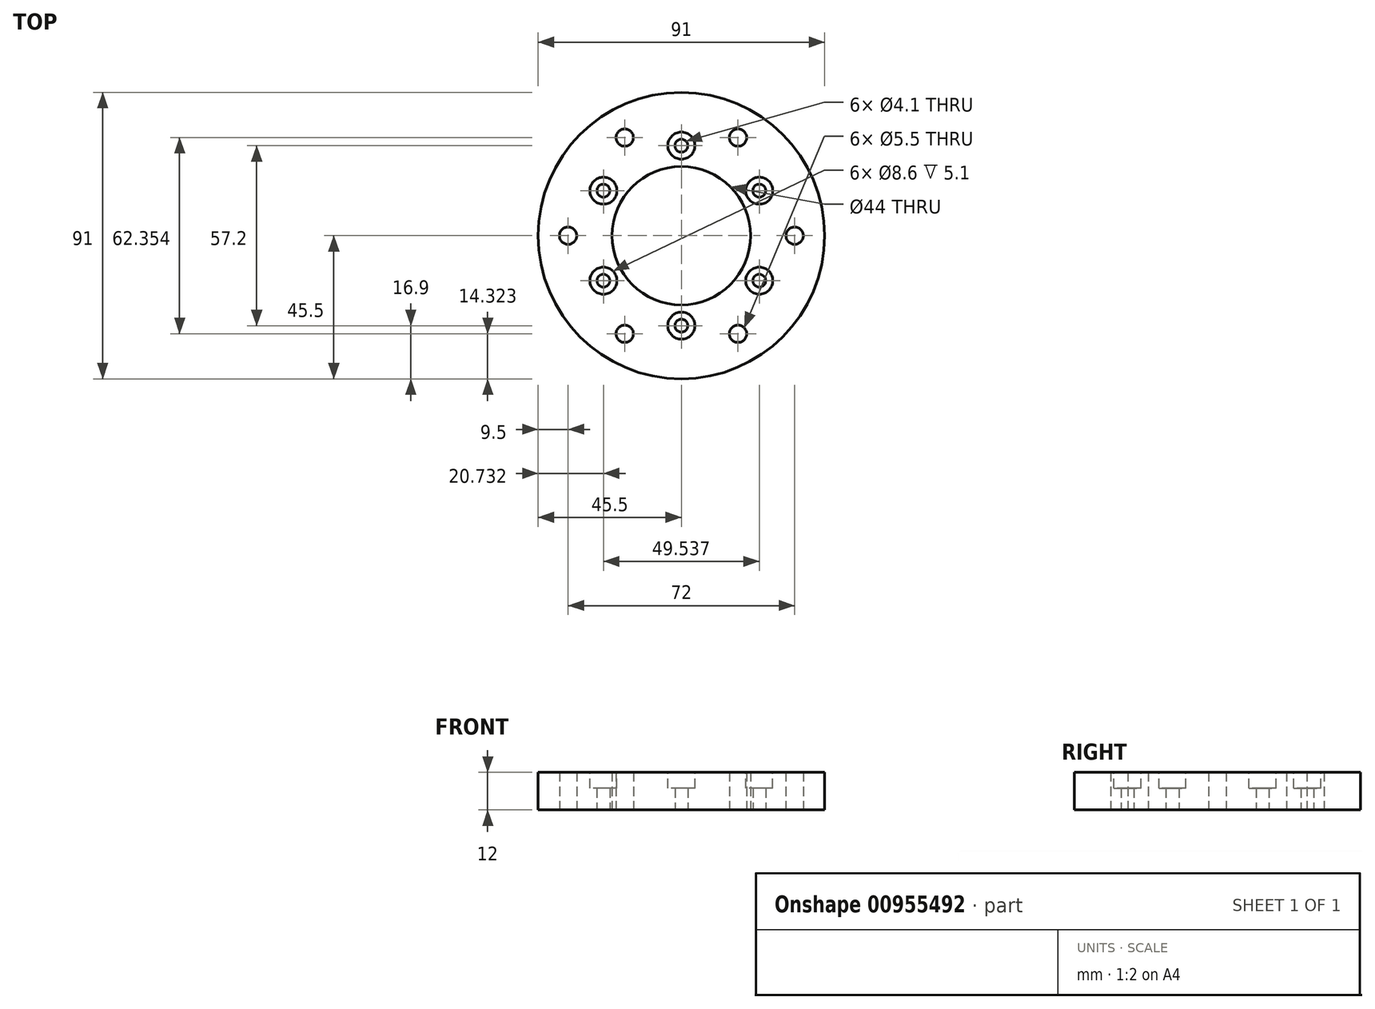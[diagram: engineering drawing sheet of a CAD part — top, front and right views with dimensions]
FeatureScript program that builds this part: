
annotation { "Feature Type Name" : "Feature", "Feature Type Description" : "" }
export const myFeature = defineFeature(function(context is Context, id is Id, definition is map)
    precondition{}
    {
        {
            var Q0;
            Q0=qCreatedBy(makeId("Top.planeOp"),FACE);
            var sketch = newSketch(context, id + "F0", { "sketchPlane" : qUnion([Q0])});
            skCircle(sketch, "E0", {"center": v(18, 31.18) * mm, "radius": 2.75 * mm});
            skCircle(sketch, "E1", {"center": v(36, 0) * mm, "radius": 2.75 * mm});
            skCircle(sketch, "E2", {"center": v(-18, 31.18) * mm, "radius": 2.75 * mm});
            skCircle(sketch, "E3", {"center": v(-36, 0) * mm, "radius": 2.75 * mm});
            skCircle(sketch, "E4", {"center": v(-18, -31.18) * mm, "radius": 2.75 * mm});
            skCircle(sketch, "E5", {"center": v(18, -31.18) * mm, "radius": 2.75 * mm});
            skCircle(sketch, "E6", {"center": v(0, 0) * mm, "radius": 45.5 * mm});
            skCircle(sketch, "E7", {"center": v(0, 28.6) * mm, "radius": 2.05 * mm});
            skCircle(sketch, "E8", {"center": v(24.77, 14.3) * mm, "radius": 2.05 * mm});
            skCircle(sketch, "E9", {"center": v(24.77, -14.3) * mm, "radius": 2.05 * mm});
            skCircle(sketch, "E10", {"center": v(0, -28.6) * mm, "radius": 2.05 * mm});
            skCircle(sketch, "E11", {"center": v(-24.77, -14.3) * mm, "radius": 2.05 * mm});
            skCircle(sketch, "E12", {"center": v(-24.77, 14.3) * mm, "radius": 2.05 * mm});
            skCircle(sketch, "E13", {"center": v(0, 0) * mm, "radius": 22 * mm});
            skSolve(sketch);
        }
        {
            var Q0;
            Q0=makeQuery(id+"F0.imprint","IMPRINT",FACE,{"disambiguationData":[TD([[makeQuery(id+"F0.imprint","IMPRINT",EDGE,{"derivedFrom":sQuery(id+"F0.wireOp",EDGE,"E6")}),1.0]])]});
            var Q1;
            {var subQ20=sQuery(id+"F0.wireOp",EDGE,"6pNGrUdh-8fK0-G4KZ-KcMA-2MZ6hp1kdz4s");var subQ32=sQuery(id+"F0.wireOp",EDGE,"E0");var subQ34=makeQuery(id+"F0.imprint","INTERSECT",VERTEX,{"disambiguationData":[OD(0.0)],"derivedFrom":[subQ20,subQ32]});Q1=makeQuery(id+"F0.imprint","IMPRINT",FACE,{"disambiguationData":[TD([[makeQuery(id+"F0.imprint","IMPRINT",EDGE,{"disambiguationData":[TD([[subQ34,1.0]])],"derivedFrom":subQ20}),1.0]])]});}
            var Q2;
            Q2=makeQuery(id+"F0.imprint","IMPRINT",FACE,{"disambiguationData":[TD([[makeQuery(id+"F0.imprint","IMPRINT",EDGE,{"derivedFrom":sQuery(id+"F0.wireOp",EDGE,"E13")}),-1.0]])]});
            extrude(context, id + "F1", {"entities" : qUnion([Q0, Q1, Q2]), "depth" : 12 * mm, "offsetDistance" : 25 * mm});
        }
        {
            var Q0;
            Q0=makeQuery(id+"F1.opExtrude","CAP_FACE",FACE,{"disambiguationData":[OSD([sQuery(id+"F0.wireOp",EDGE,"E0"),sQuery(id+"F0.wireOp",EDGE,"E1"),sQuery(id+"F0.wireOp",EDGE,"E2"),sQuery(id+"F0.wireOp",EDGE,"E3"),sQuery(id+"F0.wireOp",EDGE,"E4"),sQuery(id+"F0.wireOp",EDGE,"E5"),sQuery(id+"F0.wireOp",EDGE,"E6"),sQuery(id+"F0.wireOp",EDGE,"E7"),sQuery(id+"F0.wireOp",EDGE,"E8"),sQuery(id+"F0.wireOp",EDGE,"E9"),sQuery(id+"F0.wireOp",EDGE,"E10"),sQuery(id+"F0.wireOp",EDGE,"E11"),sQuery(id+"F0.wireOp",EDGE,"E12"),sQuery(id+"F0.wireOp",EDGE,"E13")])],"isStart":false});
            var sketch = newSketch(context, id + "F2", { "sketchPlane" : qUnion([Q0])});
            skCircle(sketch, "E14", {"center": v(0, 0) * mm, "radius": 28.6 * mm});
            skCircle(sketch, "E15", {"center": v(0, 28.6) * mm, "radius": 4.3 * mm});
            skCircle(sketch, "E16", {"center": v(24.77, 14.3) * mm, "radius": 4.3 * mm});
            skCircle(sketch, "E17", {"center": v(24.77, -14.3) * mm, "radius": 4.3 * mm});
            skCircle(sketch, "E18", {"center": v(0, -28.6) * mm, "radius": 4.3 * mm});
            skCircle(sketch, "E19", {"center": v(-24.77, -14.3) * mm, "radius": 4.3 * mm});
            skCircle(sketch, "E20", {"center": v(-24.77, 14.3) * mm, "radius": 4.3 * mm});
            skSolve(sketch);
        }
        {
            var Q0;
            {var subQ0=sQuery(id+"F2.wireOp",EDGE,"E20");var subQ1=sQuery(id+"F2.wireOp",EDGE,"E14");var subQ2=makeQuery(id+"F2.imprint","INTERSECT",VERTEX,{"disambiguationData":[OD(0.0)],"derivedFrom":[subQ1,subQ0]});Q0=makeQuery(id+"F2.imprint","IMPRINT",FACE,{"disambiguationData":[TD([[makeQuery(id+"F2.imprint","IMPRINT",EDGE,{"disambiguationData":[TD([[subQ2,-1.0]])],"derivedFrom":subQ1}),1.0]])]});}
            var Q1;
            {var subQ0=sQuery(id+"F2.wireOp",EDGE,"E20");var subQ1=sQuery(id+"F2.wireOp",EDGE,"E14");var subQ2=makeQuery(id+"F2.imprint","INTERSECT",VERTEX,{"disambiguationData":[OD(0.0)],"derivedFrom":[subQ1,subQ0]});Q1=makeQuery(id+"F2.imprint","IMPRINT",FACE,{"disambiguationData":[TD([[makeQuery(id+"F2.imprint","IMPRINT",EDGE,{"disambiguationData":[TD([[subQ2,-1.0]])],"derivedFrom":subQ1}),-1.0]])]});}
            var Q2;
            {var subQ0=sQuery(id+"F2.wireOp",EDGE,"E15");var subQ1=sQuery(id+"F2.wireOp",EDGE,"E14");var subQ2=makeQuery(id+"F2.imprint","INTERSECT",VERTEX,{"disambiguationData":[OD(0.0)],"derivedFrom":[subQ1,subQ0]});Q2=makeQuery(id+"F2.imprint","IMPRINT",FACE,{"disambiguationData":[TD([[makeQuery(id+"F2.imprint","IMPRINT",EDGE,{"disambiguationData":[TD([[subQ2,-1.0]])],"derivedFrom":subQ1}),-1.0]])]});}
            var Q3;
            {var subQ0=sQuery(id+"F2.wireOp",EDGE,"E15");var subQ1=sQuery(id+"F2.wireOp",EDGE,"E14");var subQ2=makeQuery(id+"F2.imprint","INTERSECT",VERTEX,{"disambiguationData":[OD(0.0)],"derivedFrom":[subQ1,subQ0]});Q3=makeQuery(id+"F2.imprint","IMPRINT",FACE,{"disambiguationData":[TD([[makeQuery(id+"F2.imprint","IMPRINT",EDGE,{"disambiguationData":[TD([[subQ2,-1.0]])],"derivedFrom":subQ1}),1.0]])]});}
            var Q4;
            {var subQ0=sQuery(id+"F2.wireOp",EDGE,"E16");var subQ1=sQuery(id+"F2.wireOp",EDGE,"E14");var subQ2=makeQuery(id+"F2.imprint","INTERSECT",VERTEX,{"disambiguationData":[OD(0.0)],"derivedFrom":[subQ1,subQ0]});Q4=makeQuery(id+"F2.imprint","IMPRINT",FACE,{"disambiguationData":[TD([[makeQuery(id+"F2.imprint","IMPRINT",EDGE,{"disambiguationData":[TD([[subQ2,-1.0]])],"derivedFrom":subQ1}),-1.0]])]});}
            var Q5;
            {var subQ0=sQuery(id+"F2.wireOp",EDGE,"E16");var subQ1=sQuery(id+"F2.wireOp",EDGE,"E14");var subQ2=makeQuery(id+"F2.imprint","INTERSECT",VERTEX,{"disambiguationData":[OD(0.0)],"derivedFrom":[subQ1,subQ0]});Q5=makeQuery(id+"F2.imprint","IMPRINT",FACE,{"disambiguationData":[TD([[makeQuery(id+"F2.imprint","IMPRINT",EDGE,{"disambiguationData":[TD([[subQ2,-1.0]])],"derivedFrom":subQ1}),1.0]])]});}
            var Q6;
            {var subQ0=sQuery(id+"F2.wireOp",EDGE,"E17");var subQ1=sQuery(id+"F2.wireOp",EDGE,"E14");var subQ2=makeQuery(id+"F2.imprint","INTERSECT",VERTEX,{"disambiguationData":[OD(0.0)],"derivedFrom":[subQ1,subQ0]});Q6=makeQuery(id+"F2.imprint","IMPRINT",FACE,{"disambiguationData":[TD([[makeQuery(id+"F2.imprint","IMPRINT",EDGE,{"disambiguationData":[TD([[subQ2,-1.0]])],"derivedFrom":subQ1}),-1.0]])]});}
            var Q7;
            {var subQ0=sQuery(id+"F2.wireOp",EDGE,"E17");var subQ1=sQuery(id+"F2.wireOp",EDGE,"E14");var subQ2=makeQuery(id+"F2.imprint","INTERSECT",VERTEX,{"disambiguationData":[OD(0.0)],"derivedFrom":[subQ1,subQ0]});Q7=makeQuery(id+"F2.imprint","IMPRINT",FACE,{"disambiguationData":[TD([[makeQuery(id+"F2.imprint","IMPRINT",EDGE,{"disambiguationData":[TD([[subQ2,-1.0]])],"derivedFrom":subQ1}),1.0]])]});}
            var Q8;
            {var subQ0=sQuery(id+"F2.wireOp",EDGE,"E18");var subQ1=sQuery(id+"F2.wireOp",EDGE,"E14");var subQ2=makeQuery(id+"F2.imprint","INTERSECT",VERTEX,{"disambiguationData":[OD(0.0)],"derivedFrom":[subQ1,subQ0]});Q8=makeQuery(id+"F2.imprint","IMPRINT",FACE,{"disambiguationData":[TD([[makeQuery(id+"F2.imprint","IMPRINT",EDGE,{"disambiguationData":[TD([[subQ2,-1.0]])],"derivedFrom":subQ1}),1.0]])]});}
            var Q9;
            {var subQ0=sQuery(id+"F2.wireOp",EDGE,"E18");var subQ1=sQuery(id+"F2.wireOp",EDGE,"E14");var subQ2=makeQuery(id+"F2.imprint","INTERSECT",VERTEX,{"disambiguationData":[OD(0.0)],"derivedFrom":[subQ1,subQ0]});Q9=makeQuery(id+"F2.imprint","IMPRINT",FACE,{"disambiguationData":[TD([[makeQuery(id+"F2.imprint","IMPRINT",EDGE,{"disambiguationData":[TD([[subQ2,-1.0]])],"derivedFrom":subQ1}),-1.0]])]});}
            var Q10;
            {var subQ0=sQuery(id+"F2.wireOp",EDGE,"E19");var subQ1=sQuery(id+"F2.wireOp",EDGE,"E14");var subQ2=makeQuery(id+"F2.imprint","INTERSECT",VERTEX,{"disambiguationData":[OD(0.0)],"derivedFrom":[subQ1,subQ0]});Q10=makeQuery(id+"F2.imprint","IMPRINT",FACE,{"disambiguationData":[TD([[makeQuery(id+"F2.imprint","IMPRINT",EDGE,{"disambiguationData":[TD([[subQ2,-1.0]])],"derivedFrom":subQ1}),1.0]])]});}
            var Q11;
            {var subQ0=sQuery(id+"F2.wireOp",EDGE,"E19");var subQ1=sQuery(id+"F2.wireOp",EDGE,"E14");var subQ2=makeQuery(id+"F2.imprint","INTERSECT",VERTEX,{"disambiguationData":[OD(0.0)],"derivedFrom":[subQ1,subQ0]});Q11=makeQuery(id+"F2.imprint","IMPRINT",FACE,{"disambiguationData":[TD([[makeQuery(id+"F2.imprint","IMPRINT",EDGE,{"disambiguationData":[TD([[subQ2,-1.0]])],"derivedFrom":subQ1}),-1.0]])]});}
            extrude(context, id + "F3", {"entities" : qUnion([Q0, Q1, Q2, Q3, Q4, Q5, Q6, Q7, Q8, Q9, Q10, Q11]), "operationType" : NewBodyOperationType.REMOVE, "oppositeDirection" : true, "depth" : 5.1 * mm, "offsetDistance" : 25 * mm});
        }
    });
